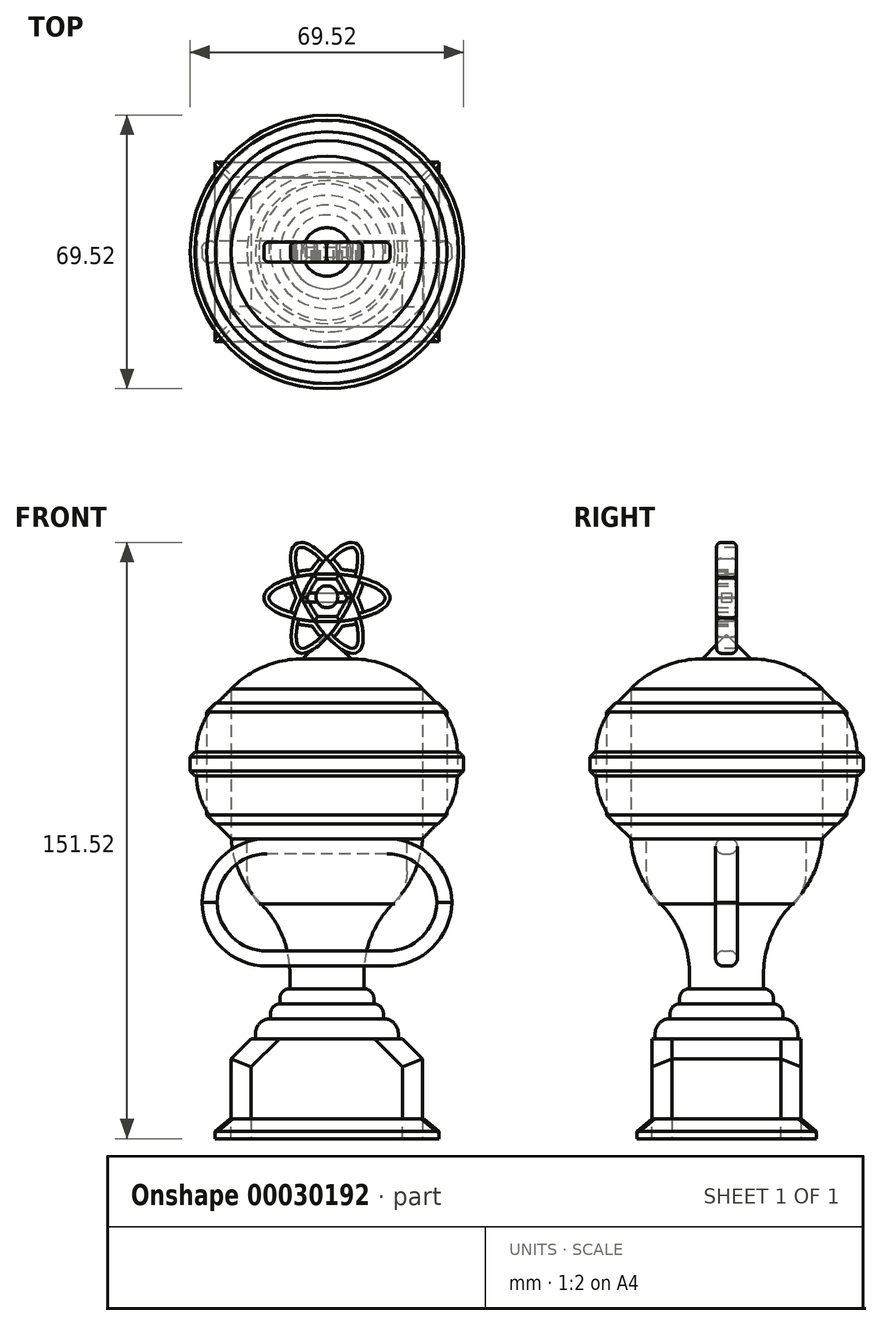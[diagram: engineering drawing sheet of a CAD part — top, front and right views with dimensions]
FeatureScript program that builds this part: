
annotation { "Feature Type Name" : "Feature", "Feature Type Description" : "" }
export const myFeature = defineFeature(function(context is Context, id is Id, definition is map)
    precondition{}
    {
        {
            var Q0;
            Q0=qCreatedBy(makeId("Top.planeOp"),FACE);
            var sketch = newSketch(context, id + "F0", { "sketchPlane" : qUnion([Q0])});
            skLineSegment(sketch, "E0.rect.bottom", {"start": v(-24.32, 18.93) * mm, "end": v(24.32, 18.93) * mm});
            skLineSegment(sketch, "E0.rect.top", {"start": v(-24.32, -18.93) * mm, "end": v(24.32, -18.93) * mm});
            skLineSegment(sketch, "E0.rect.left", {"start": v(-24.32, 18.93) * mm, "end": v(-24.32, -18.93) * mm});
            skLineSegment(sketch, "E0.rect.right", {"start": v(24.32, 18.93) * mm, "end": v(24.32, -18.93) * mm});
            skPoint(sketch, "E0.rect.middle", {"position": v(0, 0) * mm});
            skSolve(sketch);
        }
        {
            var Q0;
            Q0=makeQuery(id+"F0.imprint","IMPRINT",FACE,{"disambiguationData":[TD([[makeQuery(id+"F0.imprint","IMPRINT",EDGE,{"derivedFrom":sQuery(id+"F0.wireOp",EDGE,"E0.rect.bottom")}),-1.0]])]});
            extrude(context, id + "F1", {"entities" : qUnion([Q0]), "oppositeDirection" : true, "depth" : 76.2 * mm, "hasSecondDirection" : true, "secondDirectionOppositeDirection" : true, "secondDirectionDepth" : 50.8 * mm});
        }
        {
            var Q0;
            Q0=qCreatedBy(makeId("Top.planeOp"),FACE);
            var sketch = newSketch(context, id + "F2", { "sketchPlane" : qUnion([Q0])});
            skCircle(sketch, "E1", {"center": v(0, 0) * mm, "radius": 18.15 * mm});
            skSolve(sketch);
        }
        {
            var Q0;
            Q0=makeQuery(id+"F2.imprint","IMPRINT",FACE,{"disambiguationData":[TD([[makeQuery(id+"F2.imprint","IMPRINT",EDGE,{"derivedFrom":sQuery(id+"F2.wireOp",EDGE,"E1")}),1.0]])]});
            extrude(context, id + "F3", {"entities" : qUnion([Q0]), "operationType" : NewBodyOperationType.ADD, "oppositeDirection" : true, "depth" : 50.8 * mm, "hasSecondDirection" : true, "secondDirectionOppositeDirection" : true, "secondDirectionDepth" : 45.72 * mm});
        }
        {
            var Q0;
            Q0=makeQuery(id+"F3.opExtrude","CAP_EDGE",EDGE,{"disambiguationData":[OSD([sQuery(id+"F2.wireOp",EDGE,"E1")])],"isStart":true});
            fillet(context, id + "F4", {"entities" : qUnion([Q0]), "radius" : 3.8 * mm, "tangentPropagation" : true, "allowEdgeOverflow" : false});
        }
        {
            var Q0;
            Q0=makeQuery(id+"F3.opExtrude","CAP_FACE",FACE,{"disambiguationData":[OSD([sQuery(id+"F2.wireOp",EDGE,"E1")])],"isStart":true});
            extrude(context, id + "F5", {"entities" : qUnion([Q0]), "operationType" : NewBodyOperationType.ADD, "depth" : 3.8 * mm});
        }
        {
            var Q0;
            Q0=makeQuery(id+"F5.opExtrude","CAP_EDGE",EDGE,{"disambiguationData":[OSD([sQuery(id+"F2.wireOp",EDGE,"E1")])],"isStart":false});
            fillet(context, id + "F6", {"entities" : qUnion([Q0]), "radius" : 2.54 * mm, "tangentPropagation" : true, "allowEdgeOverflow" : false});
        }
        {
            var Q0;
            Q0=qCreatedBy(makeId("Top.planeOp"),FACE);
            var sketch = newSketch(context, id + "F7", { "sketchPlane" : qUnion([Q0])});
            skCircle(sketch, "E2", {"center": v(0, 0) * mm, "radius": 11.95 * mm});
            skSolve(sketch);
        }
        {
            var Q0;
            Q0=makeQuery(id+"F7.imprint","IMPRINT",FACE,{"disambiguationData":[TD([[makeQuery(id+"F7.imprint","IMPRINT",EDGE,{"derivedFrom":sQuery(id+"F7.wireOp",EDGE,"E2")}),1.0]])]});
            extrude(context, id + "F8", {"entities" : qUnion([Q0]), "operationType" : NewBodyOperationType.ADD, "oppositeDirection" : true, "depth" : 43.18 * mm, "hasSecondDirection" : true, "secondDirectionOppositeDirection" : true, "secondDirectionDepth" : 38.1 * mm});
        }
        {
            var Q0;
            Q0=makeQuery(id+"F8.opExtrude","CAP_EDGE",EDGE,{"disambiguationData":[OSD([sQuery(id+"F7.wireOp",EDGE,"E2")])],"isStart":true});
            fillet(context, id + "F9", {"entities" : qUnion([Q0]), "radius" : 2.54 * mm, "tangentPropagation" : true, "allowEdgeOverflow" : false});
        }
        {
            var Q0;
            Q0=qCreatedBy(makeId("Top.planeOp"),FACE);
            var sketch = newSketch(context, id + "F10", { "sketchPlane" : qUnion([Q0])});
            skCircle(sketch, "E3", {"center": v(0, 0) * mm, "radius": 24.35 * mm});
            skSolve(sketch);
        }
        {
            var Q0;
            Q0=makeQuery(id+"F8.opExtrude","CAP_FACE",FACE,{"disambiguationData":[OSD([sQuery(id+"F7.wireOp",EDGE,"E2")])],"isStart":true});
            extrude(context, id + "F11", {"entities" : qUnion([Q0]), "depth" : 15.24 * mm});
        }
        {
            var Q0;
            Q0=makeQuery(id+"F10.imprint","IMPRINT",FACE,{"disambiguationData":[TD([[makeQuery(id+"F10.imprint","IMPRINT",EDGE,{"derivedFrom":sQuery(id+"F10.wireOp",EDGE,"E3")}),1.0]])]});
            extrude(context, id + "F12", {"entities" : qUnion([Q0]), "operationType" : NewBodyOperationType.ADD, "oppositeDirection" : true, "depth" : 24.13 * mm, "hasDraft" : true, "draftAngle" : 0 * degree});
        }
        {
            var Q0;
            Q0=makeQuery(id+"F12.opExtrude","CAP_EDGE",EDGE,{"disambiguationData":[OSD([sQuery(id+"F10.wireOp",EDGE,"E3")])],"isStart":false});
            chamfer(context, id + "F13", {"entities" : qUnion([Q0]), "width" : 15.24 * mm, "tangentPropagation" : true});
        }
        {
            var Q0;
            {var subQ0=sQuery(id+"F10.wireOp",EDGE,"E3");Q0=makeQuery(id+"F13.opChamfer","BLEND_EDGE",EDGE,{"blendedFrom":[makeQuery(id+"F12.opExtrude","CAP_EDGE",EDGE,{"disambiguationData":[OSD([subQ0])],"isStart":false}),makeQuery(id+"F12.opExtrude","SWEPT_FACE",FACE,{"disambiguationData":[OSD([subQ0])]})],"blendedInto":[makeQuery(id+"F12.opExtrude","SWEPT_FACE",FACE,{"disambiguationData":[OSD([subQ0])]})]});}
            var Q1;
            Q1=makeQuery(id+"F13.opChamfer","BLEND_EDGE",EDGE,{"blendedFrom":[makeQuery(id+"F12.opExtrude","CAP_EDGE",EDGE,{"disambiguationData":[OSD([sQuery(id+"F10.wireOp",EDGE,"E3")])],"isStart":false}),makeQuery(id+"F11.opExtrude","SWEPT_FACE",FACE,{"disambiguationData":[OSD([sQuery(id+"F7.wireOp",EDGE,"E2")])]})],"blendedInto":[makeQuery(id+"F11.opExtrude","SWEPT_FACE",FACE,{"disambiguationData":[OSD([sQuery(id+"F7.wireOp",EDGE,"E2")])]})]});
            fillet(context, id + "F14", {"entities" : qUnion([Q0, Q1]), "radius" : 25.4 * mm, "tangentPropagation" : true, "allowEdgeOverflow" : false});
        }
        {
            var Q0;
            Q0=makeQuery(id+"F12.opExtrude","CAP_FACE",FACE,{"disambiguationData":[OSD([sQuery(id+"F10.wireOp",EDGE,"E3")])],"isStart":true});
            extrude(context, id + "F15", {"entities" : qUnion([Q0]), "depth" : 38.1 * mm});
        }
        {
            var Q0;
            Q0=makeQuery(id+"F15.opExtrude","CAP_FACE",FACE,{"disambiguationData":[OSD([sQuery(id+"F10.wireOp",EDGE,"E3")])],"isStart":false});
            extrude(context, id + "F16", {"entities" : qUnion([Q0]), "operationType" : NewBodyOperationType.ADD, "depth" : 7.62 * mm, "hasDraft" : true, "draftAngle" : 45 * degree, "draftPullDirection" : true});
        }
        {
            var Q0;
            Q0=makeQuery(id+"F16.opExtrude","CAP_EDGE",EDGE,{"disambiguationData":[OSD([sQuery(id+"F10.wireOp",EDGE,"E3")])],"isStart":false});
            fillet(context, id + "F17", {"entities" : qUnion([Q0]), "radius" : 25.4 * mm, "tangentPropagation" : true, "allowEdgeOverflow" : false});
        }
        {
            var Q0;
            Q0=qCreatedBy(makeId("Front.planeOp"),FACE);
            var sketch = newSketch(context, id + "F18", { "sketchPlane" : qUnion([Q0])});
            skEllipse(sketch, "E4", {"center": v(0, 61.22) * mm, "majorRadius": 16.03 * mm, "minorRadius": 6.08 * mm, "majorAxis": v(1, 0)});
            skEllipse(sketch, "E5", {"center": v(0, 61.22) * mm, "majorRadius": 15.7 * mm, "minorRadius": 5.85 * mm, "majorAxis": v(0.48, 0.88)});
            skEllipse(sketch, "E6", {"center": v(0, 61.22) * mm, "majorRadius": 15.84 * mm, "minorRadius": 5.77 * mm, "majorAxis": v(0.49, -0.87)});
            skSolve(sketch);
        }
        {
            var Q0;
            {var subQ0=sQuery(id+"F18.wireOp",EDGE,"E6");var subQ3=sQuery(id+"F18.wireOp",EDGE,"E4");var subQ4=makeQuery(id+"F18.imprint","INTERSECT",VERTEX,{"disambiguationData":[OD(0.0)],"derivedFrom":[subQ3,subQ0]});Q0=makeQuery(id+"F18.imprint","IMPRINT",FACE,{"disambiguationData":[TD([[makeQuery(id+"F18.imprint","IMPRINT",EDGE,{"disambiguationData":[TD([[subQ4,1.0]])],"derivedFrom":subQ3}),-1.0]])]});}
            var Q1;
            {var subQ0=sQuery(id+"F18.wireOp",EDGE,"E6");var subQ3=sQuery(id+"F18.wireOp",EDGE,"E4");var subQ7=makeQuery(id+"F18.imprint","INTERSECT",VERTEX,{"disambiguationData":[OD(2.0)],"derivedFrom":[subQ3,subQ0]});Q1=makeQuery(id+"F18.imprint","IMPRINT",FACE,{"disambiguationData":[TD([[makeQuery(id+"F18.imprint","IMPRINT",EDGE,{"disambiguationData":[TD([[subQ7,-1.0]])],"derivedFrom":subQ3}),1.0]])]});}
            var Q2;
            {var subQ1=sQuery(id+"F18.wireOp",EDGE,"E4");var subQ3=sQuery(id+"F18.wireOp",EDGE,"E5");var subQ5=makeQuery(id+"F18.imprint","INTERSECT",VERTEX,{"disambiguationData":[OD(0.0)],"derivedFrom":[subQ1,subQ3]});Q2=makeQuery(id+"F18.imprint","IMPRINT",FACE,{"disambiguationData":[TD([[makeQuery(id+"F18.imprint","IMPRINT",EDGE,{"disambiguationData":[TD([[subQ5,-1.0]])],"derivedFrom":subQ1}),-1.0]])]});}
            var Q3;
            {var subQ1=sQuery(id+"F18.wireOp",EDGE,"E5");var subQ3=sQuery(id+"F18.wireOp",EDGE,"E4");var subQ5=makeQuery(id+"F18.imprint","INTERSECT",VERTEX,{"disambiguationData":[OD(0.0)],"derivedFrom":[subQ3,subQ1]});Q3=makeQuery(id+"F18.imprint","IMPRINT",FACE,{"disambiguationData":[TD([[makeQuery(id+"F18.imprint","IMPRINT",EDGE,{"disambiguationData":[TD([[subQ5,1.0]])],"derivedFrom":subQ3}),1.0]])]});}
            var Q4;
            {var subQ0=sQuery(id+"F18.wireOp",EDGE,"E6");var subQ3=sQuery(id+"F18.wireOp",EDGE,"E4");var subQ4=makeQuery(id+"F18.imprint","INTERSECT",VERTEX,{"disambiguationData":[OD(1.0)],"derivedFrom":[subQ3,subQ0]});Q4=makeQuery(id+"F18.imprint","IMPRINT",FACE,{"disambiguationData":[TD([[makeQuery(id+"F18.imprint","IMPRINT",EDGE,{"disambiguationData":[TD([[subQ4,1.0]])],"derivedFrom":subQ3}),-1.0]])]});}
            var Q5;
            {var subQ1=sQuery(id+"F18.wireOp",EDGE,"E4");var subQ3=sQuery(id+"F18.wireOp",EDGE,"E5");var subQ5=makeQuery(id+"F18.imprint","INTERSECT",VERTEX,{"disambiguationData":[OD(1.0)],"derivedFrom":[subQ1,subQ3]});Q5=makeQuery(id+"F18.imprint","IMPRINT",FACE,{"disambiguationData":[TD([[makeQuery(id+"F18.imprint","IMPRINT",EDGE,{"disambiguationData":[TD([[subQ5,-1.0]])],"derivedFrom":subQ1}),-1.0]])]});}
            var Q6;
            {var subQ0=sQuery(id+"F18.wireOp",EDGE,"E6");var subQ3=sQuery(id+"F18.wireOp",EDGE,"E4");var subQ4=makeQuery(id+"F18.imprint","INTERSECT",VERTEX,{"disambiguationData":[OD(0.0)],"derivedFrom":[subQ3,subQ0]});Q6=makeQuery(id+"F18.imprint","IMPRINT",FACE,{"disambiguationData":[TD([[makeQuery(id+"F18.imprint","IMPRINT",EDGE,{"disambiguationData":[TD([[subQ4,-1.0]])],"derivedFrom":subQ3}),1.0]])]});}
            extrude(context, id + "F19", {"entities" : qUnion([Q0, Q1, Q2, Q3, Q4, Q5, Q6]), "endBound" : BoundingType.SYMMETRIC, "depth" : 5.08 * mm});
        }
        {
            var Q0;
            Q0=qCreatedBy(makeId("Top.planeOp"),FACE);
            var sketch = newSketch(context, id + "F20", { "sketchPlane" : qUnion([Q0])});
            skCircle(sketch, "E7", {"center": v(0, 0) * mm, "radius": 33.14 * mm});
            skSolve(sketch);
        }
        {
            var Q0;
            Q0=makeQuery(id+"F20.imprint","IMPRINT",FACE,{"disambiguationData":[TD([[makeQuery(id+"F20.imprint","IMPRINT",EDGE,{"derivedFrom":sQuery(id+"F20.wireOp",EDGE,"E7")}),1.0]])]});
            extrude(context, id + "F21", {"entities" : qUnion([Q0]), "depth" : 38.1 * mm});
        }
        {
            var Q0;
            Q0=makeQuery(id+"F21.opExtrude","CAP_EDGE",EDGE,{"disambiguationData":[OSD([sQuery(id+"F20.wireOp",EDGE,"E7")])],"isStart":false});
            var Q1;
            Q1=makeQuery(id+"F21.opExtrude","CAP_EDGE",EDGE,{"disambiguationData":[OSD([sQuery(id+"F20.wireOp",EDGE,"E7")])],"isStart":true});
            chamfer(context, id + "F22", {"entities" : qUnion([Q0, Q1]), "width" : 8.9 * mm, "tangentPropagation" : true});
        }
        {
            var Q0;
            {var subQ0=sQuery(id+"F20.wireOp",EDGE,"E7");Q0=makeQuery(id+"F22.opChamfer","BLEND_EDGE",EDGE,{"blendedFrom":[makeQuery(id+"F21.opExtrude","CAP_EDGE",EDGE,{"disambiguationData":[OSD([subQ0])],"isStart":false}),makeQuery(id+"F21.opExtrude","SWEPT_FACE",FACE,{"disambiguationData":[OSD([subQ0])]})],"blendedInto":[makeQuery(id+"F21.opExtrude","SWEPT_FACE",FACE,{"disambiguationData":[OSD([subQ0])]})]});}
            var Q1;
            {var subQ0=sQuery(id+"F20.wireOp",EDGE,"E7");Q1=makeQuery(id+"F22.opChamfer","BLEND_EDGE",EDGE,{"blendedFrom":[makeQuery(id+"F21.opExtrude","CAP_EDGE",EDGE,{"disambiguationData":[OSD([subQ0])],"isStart":true}),makeQuery(id+"F21.opExtrude","SWEPT_FACE",FACE,{"disambiguationData":[OSD([subQ0])]})],"blendedInto":[makeQuery(id+"F21.opExtrude","SWEPT_FACE",FACE,{"disambiguationData":[OSD([subQ0])]})]});}
            fillet(context, id + "F23", {"entities" : qUnion([Q0, Q1]), "radius" : 17.78 * mm, "tangentPropagation" : true, "allowEdgeOverflow" : false});
        }
        {
            var Q0;
            Q0=makeQuery(id+"F16.opExtrude","CAP_FACE",FACE,{"disambiguationData":[OSD([sQuery(id+"F10.wireOp",EDGE,"E3")])],"isStart":false});
            extrude(context, id + "F24", {"entities" : qUnion([Q0]), "depth" : 6.35 * mm, "hasDraft" : true, "draftAngle" : 45 * degree, "draftPullDirection" : true});
        }
        {
            var Q0;
            {var subQ0=sQuery(id+"F18.wireOp",EDGE,"E4");var subQ1=sQuery(id+"F18.wireOp",EDGE,"E5");var subQ2=sQuery(id+"F18.wireOp",EDGE,"E6");var subQ4=makeQuery(id+"F18.imprint","INTERSECT",VERTEX,{"disambiguationData":[OD(0.0)],"derivedFrom":[subQ0,subQ2]});var subQ5=makeQuery(id+"F18.imprint","INTERSECT",VERTEX,{"disambiguationData":[OD(0.0)],"derivedFrom":[subQ1,subQ2]});Q0=makeQuery(id+"F19.opExtrude","CAP_FACE",FACE,{"disambiguationData":[OSD([subQ0,subQ1,subQ2]),TDD([makeQuery(id+"F18.imprint","IMPRINT",EDGE,{"disambiguationData":[TD([[subQ4,1.0]])],"derivedFrom":subQ0}),makeQuery(id+"F18.imprint","IMPRINT",EDGE,{"disambiguationData":[TD([[subQ5,-1.0]])],"derivedFrom":subQ1}),makeQuery(id+"F18.imprint","IMPRINT",EDGE,{"disambiguationData":[TD([[subQ4,1.0]])],"derivedFrom":subQ2})])],"isStart":false});}
            var Q1;
            {var subQ0=sQuery(id+"F18.wireOp",EDGE,"E4");var subQ1=sQuery(id+"F18.wireOp",EDGE,"E5");var subQ2=sQuery(id+"F18.wireOp",EDGE,"E6");var subQ4=makeQuery(id+"F18.imprint","INTERSECT",VERTEX,{"disambiguationData":[OD(0.0)],"derivedFrom":[subQ0,subQ1]});var subQ5=makeQuery(id+"F18.imprint","INTERSECT",VERTEX,{"disambiguationData":[OD(0.0)],"derivedFrom":[subQ1,subQ2]});Q1=makeQuery(id+"F19.opExtrude","CAP_FACE",FACE,{"disambiguationData":[OSD([subQ0,subQ1,subQ2]),TDD([makeQuery(id+"F18.imprint","IMPRINT",EDGE,{"disambiguationData":[TD([[subQ4,-1.0]])],"derivedFrom":subQ0}),makeQuery(id+"F18.imprint","IMPRINT",EDGE,{"disambiguationData":[TD([[subQ4,-1.0]])],"derivedFrom":subQ1}),makeQuery(id+"F18.imprint","IMPRINT",EDGE,{"disambiguationData":[TD([[subQ5,1.0]])],"derivedFrom":subQ2})])],"isStart":false});}
            var Q2;
            {var subQ0=sQuery(id+"F18.wireOp",EDGE,"E4");var subQ1=sQuery(id+"F18.wireOp",EDGE,"E5");var subQ2=sQuery(id+"F18.wireOp",EDGE,"E6");var subQ3=makeQuery(id+"F18.imprint","INTERSECT",VERTEX,{"disambiguationData":[OD(2.0)],"derivedFrom":[subQ0,subQ1]});var subQ4=makeQuery(id+"F18.imprint","INTERSECT",VERTEX,{"disambiguationData":[OD(2.0)],"derivedFrom":[subQ0,subQ2]});var subQ5=makeQuery(id+"F18.imprint","INTERSECT",VERTEX,{"disambiguationData":[OD(3.0)],"derivedFrom":[subQ0,subQ1]});var subQ6=makeQuery(id+"F18.imprint","INTERSECT",VERTEX,{"disambiguationData":[OD(3.0)],"derivedFrom":[subQ0,subQ2]});Q2=makeQuery(id+"F19.opExtrude","CAP_FACE",FACE,{"disambiguationData":[OSD([subQ0,subQ1,subQ2]),TDD([makeQuery(id+"F18.imprint","IMPRINT",EDGE,{"disambiguationData":[TD([[subQ4,-1.0]])],"derivedFrom":subQ0}),makeQuery(id+"F18.imprint","IMPRINT",EDGE,{"disambiguationData":[TD([[subQ6,-1.0]])],"derivedFrom":subQ0}),makeQuery(id+"F18.imprint","IMPRINT",EDGE,{"disambiguationData":[TD([[subQ3,-1.0]])],"derivedFrom":subQ1}),makeQuery(id+"F18.imprint","IMPRINT",EDGE,{"disambiguationData":[TD([[subQ5,-1.0]])],"derivedFrom":subQ1}),makeQuery(id+"F18.imprint","IMPRINT",EDGE,{"disambiguationData":[TD([[subQ4,1.0]])],"derivedFrom":subQ2}),makeQuery(id+"F18.imprint","IMPRINT",EDGE,{"disambiguationData":[TD([[subQ6,1.0]])],"derivedFrom":subQ2})])],"isStart":false});}
            var Q3;
            {var subQ0=sQuery(id+"F18.wireOp",EDGE,"E4");var subQ1=sQuery(id+"F18.wireOp",EDGE,"E5");var subQ2=sQuery(id+"F18.wireOp",EDGE,"E6");var subQ4=makeQuery(id+"F18.imprint","INTERSECT",VERTEX,{"disambiguationData":[OD(1.0)],"derivedFrom":[subQ0,subQ1]});var subQ5=makeQuery(id+"F18.imprint","INTERSECT",VERTEX,{"disambiguationData":[OD(1.0)],"derivedFrom":[subQ1,subQ2]});Q3=makeQuery(id+"F19.opExtrude","CAP_FACE",FACE,{"disambiguationData":[OSD([subQ0,subQ1,subQ2]),TDD([makeQuery(id+"F18.imprint","IMPRINT",EDGE,{"disambiguationData":[TD([[subQ4,-1.0]])],"derivedFrom":subQ0}),makeQuery(id+"F18.imprint","IMPRINT",EDGE,{"disambiguationData":[TD([[subQ4,-1.0]])],"derivedFrom":subQ1}),makeQuery(id+"F18.imprint","IMPRINT",EDGE,{"disambiguationData":[TD([[subQ5,1.0]])],"derivedFrom":subQ2})])],"isStart":false});}
            var Q4;
            {var subQ0=sQuery(id+"F18.wireOp",EDGE,"E4");var subQ1=sQuery(id+"F18.wireOp",EDGE,"E5");var subQ2=sQuery(id+"F18.wireOp",EDGE,"E6");var subQ3=makeQuery(id+"F18.imprint","INTERSECT",VERTEX,{"disambiguationData":[OD(1.0)],"derivedFrom":[subQ0,subQ2]});var subQ4=makeQuery(id+"F18.imprint","INTERSECT",VERTEX,{"disambiguationData":[OD(0.0)],"derivedFrom":[subQ0,subQ1]});Q4=makeQuery(id+"F19.opExtrude","CAP_FACE",FACE,{"disambiguationData":[OSD([subQ0,subQ1,subQ2]),TDD([makeQuery(id+"F18.imprint","IMPRINT",EDGE,{"disambiguationData":[TD([[subQ4,1.0]])],"derivedFrom":subQ0}),makeQuery(id+"F18.imprint","IMPRINT",EDGE,{"disambiguationData":[TD([[subQ4,1.0]])],"derivedFrom":subQ1}),makeQuery(id+"F18.imprint","IMPRINT",EDGE,{"disambiguationData":[TD([[subQ3,-1.0]])],"derivedFrom":subQ2})])],"isStart":false});}
            var Q5;
            {var subQ0=sQuery(id+"F18.wireOp",EDGE,"E4");var subQ1=sQuery(id+"F18.wireOp",EDGE,"E5");var subQ2=sQuery(id+"F18.wireOp",EDGE,"E6");var subQ3=makeQuery(id+"F18.imprint","INTERSECT",VERTEX,{"disambiguationData":[OD(1.0)],"derivedFrom":[subQ0,subQ1]});var subQ4=makeQuery(id+"F18.imprint","INTERSECT",VERTEX,{"disambiguationData":[OD(0.0)],"derivedFrom":[subQ0,subQ2]});Q5=makeQuery(id+"F19.opExtrude","CAP_FACE",FACE,{"disambiguationData":[OSD([subQ0,subQ1,subQ2]),TDD([makeQuery(id+"F18.imprint","IMPRINT",EDGE,{"disambiguationData":[TD([[subQ4,-1.0]])],"derivedFrom":subQ0}),makeQuery(id+"F18.imprint","IMPRINT",EDGE,{"disambiguationData":[TD([[subQ3,1.0]])],"derivedFrom":subQ1}),makeQuery(id+"F18.imprint","IMPRINT",EDGE,{"disambiguationData":[TD([[subQ4,-1.0]])],"derivedFrom":subQ2})])],"isStart":true});}
            var Q6;
            {var subQ0=sQuery(id+"F18.wireOp",EDGE,"E4");var subQ1=sQuery(id+"F18.wireOp",EDGE,"E5");var subQ2=sQuery(id+"F18.wireOp",EDGE,"E6");var subQ4=makeQuery(id+"F18.imprint","INTERSECT",VERTEX,{"disambiguationData":[OD(0.0)],"derivedFrom":[subQ0,subQ2]});var subQ5=makeQuery(id+"F18.imprint","INTERSECT",VERTEX,{"disambiguationData":[OD(0.0)],"derivedFrom":[subQ1,subQ2]});Q6=makeQuery(id+"F19.opExtrude","CAP_FACE",FACE,{"disambiguationData":[OSD([subQ0,subQ1,subQ2]),TDD([makeQuery(id+"F18.imprint","IMPRINT",EDGE,{"disambiguationData":[TD([[subQ4,1.0]])],"derivedFrom":subQ0}),makeQuery(id+"F18.imprint","IMPRINT",EDGE,{"disambiguationData":[TD([[subQ5,-1.0]])],"derivedFrom":subQ1}),makeQuery(id+"F18.imprint","IMPRINT",EDGE,{"disambiguationData":[TD([[subQ4,1.0]])],"derivedFrom":subQ2})])],"isStart":true});}
            var Q7;
            {var subQ0=sQuery(id+"F18.wireOp",EDGE,"E4");var subQ1=sQuery(id+"F18.wireOp",EDGE,"E5");var subQ2=sQuery(id+"F18.wireOp",EDGE,"E6");var subQ4=makeQuery(id+"F18.imprint","INTERSECT",VERTEX,{"disambiguationData":[OD(0.0)],"derivedFrom":[subQ0,subQ1]});var subQ5=makeQuery(id+"F18.imprint","INTERSECT",VERTEX,{"disambiguationData":[OD(0.0)],"derivedFrom":[subQ1,subQ2]});Q7=makeQuery(id+"F19.opExtrude","CAP_FACE",FACE,{"disambiguationData":[OSD([subQ0,subQ1,subQ2]),TDD([makeQuery(id+"F18.imprint","IMPRINT",EDGE,{"disambiguationData":[TD([[subQ4,-1.0]])],"derivedFrom":subQ0}),makeQuery(id+"F18.imprint","IMPRINT",EDGE,{"disambiguationData":[TD([[subQ4,-1.0]])],"derivedFrom":subQ1}),makeQuery(id+"F18.imprint","IMPRINT",EDGE,{"disambiguationData":[TD([[subQ5,1.0]])],"derivedFrom":subQ2})])],"isStart":true});}
            var Q8;
            {var subQ0=sQuery(id+"F18.wireOp",EDGE,"E4");var subQ1=sQuery(id+"F18.wireOp",EDGE,"E5");var subQ2=sQuery(id+"F18.wireOp",EDGE,"E6");var subQ3=makeQuery(id+"F18.imprint","INTERSECT",VERTEX,{"disambiguationData":[OD(1.0)],"derivedFrom":[subQ0,subQ2]});var subQ4=makeQuery(id+"F18.imprint","INTERSECT",VERTEX,{"disambiguationData":[OD(0.0)],"derivedFrom":[subQ0,subQ1]});Q8=makeQuery(id+"F19.opExtrude","CAP_FACE",FACE,{"disambiguationData":[OSD([subQ0,subQ1,subQ2]),TDD([makeQuery(id+"F18.imprint","IMPRINT",EDGE,{"disambiguationData":[TD([[subQ4,1.0]])],"derivedFrom":subQ0}),makeQuery(id+"F18.imprint","IMPRINT",EDGE,{"disambiguationData":[TD([[subQ4,1.0]])],"derivedFrom":subQ1}),makeQuery(id+"F18.imprint","IMPRINT",EDGE,{"disambiguationData":[TD([[subQ3,-1.0]])],"derivedFrom":subQ2})])],"isStart":true});}
            var Q9;
            {var subQ0=sQuery(id+"F18.wireOp",EDGE,"E4");var subQ1=sQuery(id+"F18.wireOp",EDGE,"E5");var subQ2=sQuery(id+"F18.wireOp",EDGE,"E6");var subQ4=makeQuery(id+"F18.imprint","INTERSECT",VERTEX,{"disambiguationData":[OD(1.0)],"derivedFrom":[subQ0,subQ2]});var subQ5=makeQuery(id+"F18.imprint","INTERSECT",VERTEX,{"disambiguationData":[OD(1.0)],"derivedFrom":[subQ1,subQ2]});Q9=makeQuery(id+"F19.opExtrude","CAP_FACE",FACE,{"disambiguationData":[OSD([subQ0,subQ1,subQ2]),TDD([makeQuery(id+"F18.imprint","IMPRINT",EDGE,{"disambiguationData":[TD([[subQ4,1.0]])],"derivedFrom":subQ0}),makeQuery(id+"F18.imprint","IMPRINT",EDGE,{"disambiguationData":[TD([[subQ5,-1.0]])],"derivedFrom":subQ1}),makeQuery(id+"F18.imprint","IMPRINT",EDGE,{"disambiguationData":[TD([[subQ4,1.0]])],"derivedFrom":subQ2})])],"isStart":true});}
            var Q10;
            {var subQ0=sQuery(id+"F18.wireOp",EDGE,"E4");var subQ1=sQuery(id+"F18.wireOp",EDGE,"E5");var subQ2=sQuery(id+"F18.wireOp",EDGE,"E6");var subQ4=makeQuery(id+"F18.imprint","INTERSECT",VERTEX,{"disambiguationData":[OD(1.0)],"derivedFrom":[subQ0,subQ1]});var subQ5=makeQuery(id+"F18.imprint","INTERSECT",VERTEX,{"disambiguationData":[OD(1.0)],"derivedFrom":[subQ1,subQ2]});Q10=makeQuery(id+"F19.opExtrude","CAP_FACE",FACE,{"disambiguationData":[OSD([subQ0,subQ1,subQ2]),TDD([makeQuery(id+"F18.imprint","IMPRINT",EDGE,{"disambiguationData":[TD([[subQ4,-1.0]])],"derivedFrom":subQ0}),makeQuery(id+"F18.imprint","IMPRINT",EDGE,{"disambiguationData":[TD([[subQ4,-1.0]])],"derivedFrom":subQ1}),makeQuery(id+"F18.imprint","IMPRINT",EDGE,{"disambiguationData":[TD([[subQ5,1.0]])],"derivedFrom":subQ2})])],"isStart":true});}
            var Q11;
            {var subQ0=sQuery(id+"F18.wireOp",EDGE,"E4");var subQ1=sQuery(id+"F18.wireOp",EDGE,"E5");var subQ2=sQuery(id+"F18.wireOp",EDGE,"E6");var subQ3=makeQuery(id+"F18.imprint","INTERSECT",VERTEX,{"disambiguationData":[OD(2.0)],"derivedFrom":[subQ0,subQ1]});var subQ4=makeQuery(id+"F18.imprint","INTERSECT",VERTEX,{"disambiguationData":[OD(2.0)],"derivedFrom":[subQ0,subQ2]});var subQ5=makeQuery(id+"F18.imprint","INTERSECT",VERTEX,{"disambiguationData":[OD(3.0)],"derivedFrom":[subQ0,subQ1]});var subQ6=makeQuery(id+"F18.imprint","INTERSECT",VERTEX,{"disambiguationData":[OD(3.0)],"derivedFrom":[subQ0,subQ2]});Q11=makeQuery(id+"F19.opExtrude","CAP_FACE",FACE,{"disambiguationData":[OSD([subQ0,subQ1,subQ2]),TDD([makeQuery(id+"F18.imprint","IMPRINT",EDGE,{"disambiguationData":[TD([[subQ4,-1.0]])],"derivedFrom":subQ0}),makeQuery(id+"F18.imprint","IMPRINT",EDGE,{"disambiguationData":[TD([[subQ6,-1.0]])],"derivedFrom":subQ0}),makeQuery(id+"F18.imprint","IMPRINT",EDGE,{"disambiguationData":[TD([[subQ3,-1.0]])],"derivedFrom":subQ1}),makeQuery(id+"F18.imprint","IMPRINT",EDGE,{"disambiguationData":[TD([[subQ5,-1.0]])],"derivedFrom":subQ1}),makeQuery(id+"F18.imprint","IMPRINT",EDGE,{"disambiguationData":[TD([[subQ4,1.0]])],"derivedFrom":subQ2}),makeQuery(id+"F18.imprint","IMPRINT",EDGE,{"disambiguationData":[TD([[subQ6,1.0]])],"derivedFrom":subQ2})])],"isStart":true});}
            var Q12;
            {var subQ0=sQuery(id+"F18.wireOp",EDGE,"E4");var subQ1=sQuery(id+"F18.wireOp",EDGE,"E5");var subQ2=sQuery(id+"F18.wireOp",EDGE,"E6");var subQ3=makeQuery(id+"F18.imprint","INTERSECT",VERTEX,{"disambiguationData":[OD(1.0)],"derivedFrom":[subQ0,subQ1]});var subQ4=makeQuery(id+"F18.imprint","INTERSECT",VERTEX,{"disambiguationData":[OD(0.0)],"derivedFrom":[subQ0,subQ2]});Q12=makeQuery(id+"F19.opExtrude","CAP_FACE",FACE,{"disambiguationData":[OSD([subQ0,subQ1,subQ2]),TDD([makeQuery(id+"F18.imprint","IMPRINT",EDGE,{"disambiguationData":[TD([[subQ4,-1.0]])],"derivedFrom":subQ0}),makeQuery(id+"F18.imprint","IMPRINT",EDGE,{"disambiguationData":[TD([[subQ3,1.0]])],"derivedFrom":subQ1}),makeQuery(id+"F18.imprint","IMPRINT",EDGE,{"disambiguationData":[TD([[subQ4,-1.0]])],"derivedFrom":subQ2})])],"isStart":false});}
            var Q13;
            {var subQ0=sQuery(id+"F18.wireOp",EDGE,"E4");var subQ1=sQuery(id+"F18.wireOp",EDGE,"E5");var subQ2=sQuery(id+"F18.wireOp",EDGE,"E6");var subQ4=makeQuery(id+"F18.imprint","INTERSECT",VERTEX,{"disambiguationData":[OD(1.0)],"derivedFrom":[subQ0,subQ2]});var subQ5=makeQuery(id+"F18.imprint","INTERSECT",VERTEX,{"disambiguationData":[OD(1.0)],"derivedFrom":[subQ1,subQ2]});Q13=makeQuery(id+"F19.opExtrude","CAP_FACE",FACE,{"disambiguationData":[OSD([subQ0,subQ1,subQ2]),TDD([makeQuery(id+"F18.imprint","IMPRINT",EDGE,{"disambiguationData":[TD([[subQ4,1.0]])],"derivedFrom":subQ0}),makeQuery(id+"F18.imprint","IMPRINT",EDGE,{"disambiguationData":[TD([[subQ5,-1.0]])],"derivedFrom":subQ1}),makeQuery(id+"F18.imprint","IMPRINT",EDGE,{"disambiguationData":[TD([[subQ4,1.0]])],"derivedFrom":subQ2})])],"isStart":false});}
            shell(context, id + "F25", {"entities" : qUnion([Q0, Q1, Q2, Q3, Q4, Q5, Q6, Q7, Q8, Q9, Q10, Q11, Q12, Q13]), "thickness" : 1.27 * mm});
        }
        {
            var Q0;
            Q0=qCreatedBy(makeId("Right.planeOp"),FACE);
            var sketch = newSketch(context, id + "F26", { "sketchPlane" : qUnion([Q0])});
            skLineSegment(sketch, "E8.rect.bottom", {"start": v(2.76, 0) * mm, "end": v(-2.76, 0) * mm});
            skLineSegment(sketch, "E8.rect.top", {"start": v(2.76, -32.34) * mm, "end": v(-2.76, -32.34) * mm});
            skLineSegment(sketch, "E8.rect.left", {"start": v(2.76, 0) * mm, "end": v(2.76, -32.34) * mm});
            skLineSegment(sketch, "E8.rect.right", {"start": v(-2.76, 0) * mm, "end": v(-2.76, -32.34) * mm});
            skPoint(sketch, "E8.rect.middle", {"position": v(0, -16.17) * mm});
            skSolve(sketch);
        }
        {
            var Q0;
            Q0=makeQuery(id+"F26.imprint","IMPRINT",FACE,{"disambiguationData":[TD([[makeQuery(id+"F26.imprint","IMPRINT",EDGE,{"derivedFrom":sQuery(id+"F26.wireOp",EDGE,"E8.rect.bottom")}),1.0]])]});
            extrude(context, id + "F27", {"entities" : qUnion([Q0]), "endBound" : BoundingType.SYMMETRIC, "depth" : 63.5 * mm});
        }
        {
            var Q0;
            Q0=makeQuery(id+"F27.opExtrude","CAP_EDGE",EDGE,{"disambiguationData":[OSD([sQuery(id+"F26.wireOp",EDGE,"E8.rect.bottom")])],"isStart":true});
            var Q1;
            Q1=makeQuery(id+"F27.opExtrude","CAP_EDGE",EDGE,{"disambiguationData":[OSD([sQuery(id+"F26.wireOp",EDGE,"E8.rect.top")])],"isStart":true});
            var Q2;
            Q2=makeQuery(id+"F27.opExtrude","CAP_EDGE",EDGE,{"disambiguationData":[OSD([sQuery(id+"F26.wireOp",EDGE,"E8.rect.bottom")])],"isStart":false});
            var Q3;
            Q3=makeQuery(id+"F27.opExtrude","CAP_EDGE",EDGE,{"disambiguationData":[OSD([sQuery(id+"F26.wireOp",EDGE,"E8.rect.top")])],"isStart":false});
            fillet(context, id + "F28", {"entities" : qUnion([Q0, Q1, Q2, Q3]), "radius" : 16.5 * mm, "tangentPropagation" : true, "allowEdgeOverflow" : false});
        }
        {
            var Q0;
            Q0=makeQuery(id+"F27.opExtrude","SWEPT_FACE",FACE,{"disambiguationData":[OSD([sQuery(id+"F26.wireOp",EDGE,"E8.rect.right")])]});
            var Q1;
            Q1=makeQuery(id+"F27.opExtrude","SWEPT_FACE",FACE,{"disambiguationData":[OSD([sQuery(id+"F26.wireOp",EDGE,"E8.rect.left")])]});
            shell(context, id + "F29", {"entities" : qUnion([Q0, Q1]), "thickness" : 3.8 * mm});
        }
        {
            var Q0;
            Q0=qCreatedBy(makeId("Top.planeOp"),FACE);
            var sketch = newSketch(context, id + "F30", { "sketchPlane" : qUnion([Q0])});
            skLineSegment(sketch, "E9.rect.bottom", {"start": v(-28.47, -22.8) * mm, "end": v(28.47, -22.8) * mm});
            skLineSegment(sketch, "E9.rect.top", {"start": v(-28.47, 22.8) * mm, "end": v(28.47, 22.8) * mm});
            skLineSegment(sketch, "E9.rect.left", {"start": v(-28.47, -22.8) * mm, "end": v(-28.47, 22.8) * mm});
            skLineSegment(sketch, "E9.rect.right", {"start": v(28.47, -22.8) * mm, "end": v(28.47, 22.8) * mm});
            skPoint(sketch, "E9.rect.middle", {"position": v(0, 0) * mm});
            skSolve(sketch);
        }
        {
            var Q0;
            Q0=makeQuery(id+"F30.imprint","IMPRINT",FACE,{"disambiguationData":[TD([[makeQuery(id+"F30.imprint","IMPRINT",EDGE,{"derivedFrom":sQuery(id+"F30.wireOp",EDGE,"E9.rect.bottom")}),1.0]])]});
            extrude(context, id + "F31", {"entities" : qUnion([Q0]), "oppositeDirection" : true, "depth" : 76.2 * mm, "hasSecondDirection" : true, "secondDirectionOppositeDirection" : true, "secondDirectionDepth" : 71.12 * mm});
        }
        {
            var Q0;
            Q0=makeQuery(id+"F31.opExtrude","CAP_EDGE",EDGE,{"disambiguationData":[OSD([sQuery(id+"F30.wireOp",EDGE,"E9.rect.bottom")])],"isStart":true});
            var Q1;
            Q1=makeQuery(id+"F31.opExtrude","CAP_EDGE",EDGE,{"disambiguationData":[OSD([sQuery(id+"F30.wireOp",EDGE,"E9.rect.left")])],"isStart":true});
            var Q2;
            Q2=makeQuery(id+"F31.opExtrude","CAP_EDGE",EDGE,{"disambiguationData":[OSD([sQuery(id+"F30.wireOp",EDGE,"E9.rect.right")])],"isStart":true});
            var Q3;
            Q3=makeQuery(id+"F31.opExtrude","CAP_EDGE",EDGE,{"disambiguationData":[OSD([sQuery(id+"F30.wireOp",EDGE,"E9.rect.top")])],"isStart":true});
            chamfer(context, id + "F32", {"entities" : qUnion([Q0, Q1, Q2, Q3]), "chamferType" : ChamferType.OFFSET_ANGLE, "width" : 3.8 * mm, "oppositeDirection" : false, "angle" : 40 * degree, "tangentPropagation" : true});
        }
        {
            var Q0;
            Q0=makeQuery(id+"F1.opExtrude","CAP_EDGE",EDGE,{"disambiguationData":[OSD([sQuery(id+"F0.wireOp",EDGE,"E0.rect.left")])],"isStart":true});
            var Q1;
            Q1=makeQuery(id+"F1.opExtrude","CAP_EDGE",EDGE,{"disambiguationData":[OSD([sQuery(id+"F0.wireOp",EDGE,"E0.rect.right")])],"isStart":true});
            chamfer(context, id + "F33", {"entities" : qUnion([Q0, Q1]), "width" : 5.08 * mm, "tangentPropagation" : true});
        }
        {
            var Q0;
            Q0=makeQuery(id+"F33.opChamfer","BLEND_EDGE",EDGE,{"blendedFrom":[makeQuery(id+"F1.opExtrude","CAP_EDGE",EDGE,{"disambiguationData":[OSD([sQuery(id+"F0.wireOp",EDGE,"E0.rect.left")])],"isStart":true}),makeQuery(id+"F1.opExtrude","SWEPT_FACE",FACE,{"disambiguationData":[OSD([sQuery(id+"F0.wireOp",EDGE,"E0.rect.top")])]})],"blendedInto":[makeQuery(id+"F1.opExtrude","SWEPT_FACE",FACE,{"disambiguationData":[OSD([sQuery(id+"F0.wireOp",EDGE,"E0.rect.top")])]})]});
            var Q1;
            Q1=makeQuery(id+"F33.opChamfer","BLEND_EDGE",EDGE,{"blendedFrom":[makeQuery(id+"F1.opExtrude","CAP_EDGE",EDGE,{"disambiguationData":[OSD([sQuery(id+"F0.wireOp",EDGE,"E0.rect.right")])],"isStart":true}),makeQuery(id+"F1.opExtrude","SWEPT_FACE",FACE,{"disambiguationData":[OSD([sQuery(id+"F0.wireOp",EDGE,"E0.rect.top")])]})],"blendedInto":[makeQuery(id+"F1.opExtrude","SWEPT_FACE",FACE,{"disambiguationData":[OSD([sQuery(id+"F0.wireOp",EDGE,"E0.rect.top")])]})]});
            var Q2;
            Q2=makeQuery(id+"F33.opChamfer","BLEND_EDGE",EDGE,{"blendedFrom":[makeQuery(id+"F1.opExtrude","CAP_EDGE",EDGE,{"disambiguationData":[OSD([sQuery(id+"F0.wireOp",EDGE,"E0.rect.left")])],"isStart":true}),makeQuery(id+"F1.opExtrude","SWEPT_FACE",FACE,{"disambiguationData":[OSD([sQuery(id+"F0.wireOp",EDGE,"E0.rect.bottom")])]})],"blendedInto":[makeQuery(id+"F1.opExtrude","SWEPT_FACE",FACE,{"disambiguationData":[OSD([sQuery(id+"F0.wireOp",EDGE,"E0.rect.bottom")])]})]});
            var Q3;
            Q3=makeQuery(id+"F33.opChamfer","BLEND_EDGE",EDGE,{"blendedFrom":[makeQuery(id+"F1.opExtrude","CAP_EDGE",EDGE,{"disambiguationData":[OSD([sQuery(id+"F0.wireOp",EDGE,"E0.rect.right")])],"isStart":true}),makeQuery(id+"F1.opExtrude","SWEPT_FACE",FACE,{"disambiguationData":[OSD([sQuery(id+"F0.wireOp",EDGE,"E0.rect.bottom")])]})],"blendedInto":[makeQuery(id+"F1.opExtrude","SWEPT_FACE",FACE,{"disambiguationData":[OSD([sQuery(id+"F0.wireOp",EDGE,"E0.rect.bottom")])]})]});
            chamfer(context, id + "F34", {"entities" : qUnion([Q0, Q1, Q2, Q3]), "width" : 5.08 * mm, "tangentPropagation" : true});
        }
        {
            var Q0;
            Q0=qCreatedBy(makeId("Top.planeOp"),FACE);
            var sketch = newSketch(context, id + "F35", { "sketchPlane" : qUnion([Q0])});
            skCircle(sketch, "E10", {"center": v(0, 0) * mm, "radius": 20.32 * mm});
            skSolve(sketch);
        }
        {
            var Q0;
            Q0=makeQuery(id+"F35.imprint","IMPRINT",FACE,{"disambiguationData":[TD([[makeQuery(id+"F35.imprint","IMPRINT",EDGE,{"derivedFrom":sQuery(id+"F35.wireOp",EDGE,"E10")}),1.0]])]});
            extrude(context, id + "F36", {"entities" : qUnion([Q0]), "oppositeDirection" : true, "depth" : 16.5 * mm});
        }
        {
            var Q0;
            Q0=qCreatedBy(makeId("Top.planeOp"),FACE);
            var sketch = newSketch(context, id + "F37", { "sketchPlane" : qUnion([Q0])});
            skCircle(sketch, "E11", {"center": v(0, 0) * mm, "radius": 30.54 * mm});
            skSolve(sketch);
        }
        {
            var Q0;
            Q0=makeQuery(id+"F37.imprint","IMPRINT",FACE,{"disambiguationData":[TD([[makeQuery(id+"F37.imprint","IMPRINT",EDGE,{"derivedFrom":sQuery(id+"F37.wireOp",EDGE,"E11")}),1.0]])]});
            extrude(context, id + "F38", {"entities" : qUnion([Q0]), "depth" : 34.54 * mm, "hasSecondDirection" : true, "secondDirectionOppositeDirection" : false, "secondDirectionDepth" : 3.8 * mm});
        }
        {
            var Q0;
            Q0=qCreatedBy(makeId("Top.planeOp"),FACE);
            var sketch = newSketch(context, id + "F39", { "sketchPlane" : qUnion([Q0])});
            skCircle(sketch, "E12", {"center": v(0, 0) * mm, "radius": 34.76 * mm});
            skSolve(sketch);
        }
        {
            var Q0;
            Q0=makeQuery(id+"F39.imprint","IMPRINT",FACE,{"disambiguationData":[TD([[makeQuery(id+"F39.imprint","IMPRINT",EDGE,{"derivedFrom":sQuery(id+"F39.wireOp",EDGE,"E12")}),1.0]])]});
            extrude(context, id + "F40", {"entities" : qUnion([Q0]), "depth" : 22.1 * mm, "hasSecondDirection" : true, "secondDirectionOppositeDirection" : false, "secondDirectionDepth" : 16 * mm});
        }
        {
            var Q0;
            {var subQ0=sQuery(id+"F18.wireOp",EDGE,"E6");Q0=makeQuery(id+"F19.opExtrude","CAP_EDGE",EDGE,{"disambiguationData":[OSD([subQ0]),TDD([makeQuery(id+"F18.imprint","IMPRINT",EDGE,{"disambiguationData":[TD([[makeQuery(id+"F18.imprint","INTERSECT",VERTEX,{"disambiguationData":[OD(0.0)],"derivedFrom":[sQuery(id+"F18.wireOp",EDGE,"E4"),subQ0]}),1.0]])],"derivedFrom":subQ0})])],"isStart":false});}
            var Q1;
            {var subQ0=sQuery(id+"F18.wireOp",EDGE,"E5");Q1=makeQuery(id+"F19.opExtrude","CAP_EDGE",EDGE,{"disambiguationData":[OSD([subQ0]),TDD([makeQuery(id+"F18.imprint","IMPRINT",EDGE,{"disambiguationData":[TD([[makeQuery(id+"F18.imprint","INTERSECT",VERTEX,{"disambiguationData":[OD(0.0)],"derivedFrom":[sQuery(id+"F18.wireOp",EDGE,"E4"),subQ0]}),-1.0]])],"derivedFrom":subQ0})])],"isStart":true});}
            var Q2;
            {var subQ0=sQuery(id+"F18.wireOp",EDGE,"E5");Q2=makeQuery(id+"F19.opExtrude","CAP_EDGE",EDGE,{"disambiguationData":[OSD([subQ0]),TDD([makeQuery(id+"F18.imprint","IMPRINT",EDGE,{"disambiguationData":[TD([[makeQuery(id+"F18.imprint","INTERSECT",VERTEX,{"disambiguationData":[OD(0.0)],"derivedFrom":[sQuery(id+"F18.wireOp",EDGE,"E4"),subQ0]}),-1.0]])],"derivedFrom":subQ0})])],"isStart":false});}
            var Q3;
            {var subQ0=sQuery(id+"F18.wireOp",EDGE,"E6");Q3=makeQuery(id+"F19.opExtrude","CAP_EDGE",EDGE,{"disambiguationData":[OSD([subQ0]),TDD([makeQuery(id+"F18.imprint","IMPRINT",EDGE,{"disambiguationData":[TD([[makeQuery(id+"F18.imprint","INTERSECT",VERTEX,{"disambiguationData":[OD(0.0)],"derivedFrom":[sQuery(id+"F18.wireOp",EDGE,"E4"),subQ0]}),1.0]])],"derivedFrom":subQ0})])],"isStart":true});}
            var Q4;
            {var subQ0=sQuery(id+"F18.wireOp",EDGE,"E4");Q4=makeQuery(id+"F19.opExtrude","CAP_EDGE",EDGE,{"disambiguationData":[OSD([subQ0]),TDD([makeQuery(id+"F18.imprint","IMPRINT",EDGE,{"disambiguationData":[TD([[makeQuery(id+"F18.imprint","INTERSECT",VERTEX,{"disambiguationData":[OD(0.0)],"derivedFrom":[subQ0,sQuery(id+"F18.wireOp",EDGE,"E6")]}),-1.0]])],"derivedFrom":subQ0})])],"isStart":true});}
            var Q5;
            {var subQ0=sQuery(id+"F18.wireOp",EDGE,"E4");Q5=makeQuery(id+"F19.opExtrude","CAP_EDGE",EDGE,{"disambiguationData":[OSD([subQ0]),TDD([makeQuery(id+"F18.imprint","IMPRINT",EDGE,{"disambiguationData":[TD([[makeQuery(id+"F18.imprint","INTERSECT",VERTEX,{"disambiguationData":[OD(0.0)],"derivedFrom":[subQ0,sQuery(id+"F18.wireOp",EDGE,"E6")]}),-1.0]])],"derivedFrom":subQ0})])],"isStart":false});}
            var Q6;
            {var subQ0=sQuery(id+"F18.wireOp",EDGE,"E5");Q6=makeQuery(id+"F19.opExtrude","CAP_EDGE",EDGE,{"disambiguationData":[OSD([subQ0]),TDD([makeQuery(id+"F18.imprint","IMPRINT",EDGE,{"disambiguationData":[TD([[makeQuery(id+"F18.imprint","INTERSECT",VERTEX,{"disambiguationData":[OD(1.0)],"derivedFrom":[sQuery(id+"F18.wireOp",EDGE,"E4"),subQ0]}),-1.0]])],"derivedFrom":subQ0})])],"isStart":true});}
            var Q7;
            {var subQ0=sQuery(id+"F18.wireOp",EDGE,"E6");Q7=makeQuery(id+"F19.opExtrude","CAP_EDGE",EDGE,{"disambiguationData":[OSD([subQ0]),TDD([makeQuery(id+"F18.imprint","IMPRINT",EDGE,{"disambiguationData":[TD([[makeQuery(id+"F18.imprint","INTERSECT",VERTEX,{"disambiguationData":[OD(1.0)],"derivedFrom":[sQuery(id+"F18.wireOp",EDGE,"E4"),subQ0]}),1.0]])],"derivedFrom":subQ0})])],"isStart":false});}
            var Q8;
            {var subQ0=sQuery(id+"F18.wireOp",EDGE,"E6");Q8=makeQuery(id+"F19.opExtrude","CAP_EDGE",EDGE,{"disambiguationData":[OSD([subQ0]),TDD([makeQuery(id+"F18.imprint","IMPRINT",EDGE,{"disambiguationData":[TD([[makeQuery(id+"F18.imprint","INTERSECT",VERTEX,{"disambiguationData":[OD(1.0)],"derivedFrom":[sQuery(id+"F18.wireOp",EDGE,"E4"),subQ0]}),1.0]])],"derivedFrom":subQ0})])],"isStart":true});}
            var Q9;
            {var subQ0=sQuery(id+"F18.wireOp",EDGE,"E4");Q9=makeQuery(id+"F19.opExtrude","CAP_EDGE",EDGE,{"disambiguationData":[OSD([subQ0]),TDD([makeQuery(id+"F18.imprint","IMPRINT",EDGE,{"disambiguationData":[TD([[makeQuery(id+"F18.imprint","INTERSECT",VERTEX,{"disambiguationData":[OD(0.0)],"derivedFrom":[subQ0,sQuery(id+"F18.wireOp",EDGE,"E5")]}),1.0]])],"derivedFrom":subQ0})])],"isStart":false});}
            var Q10;
            {var subQ0=sQuery(id+"F18.wireOp",EDGE,"E4");Q10=makeQuery(id+"F19.opExtrude","CAP_EDGE",EDGE,{"disambiguationData":[OSD([subQ0]),TDD([makeQuery(id+"F18.imprint","IMPRINT",EDGE,{"disambiguationData":[TD([[makeQuery(id+"F18.imprint","INTERSECT",VERTEX,{"disambiguationData":[OD(0.0)],"derivedFrom":[subQ0,sQuery(id+"F18.wireOp",EDGE,"E5")]}),1.0]])],"derivedFrom":subQ0})])],"isStart":true});}
            var Q11;
            {var subQ0=sQuery(id+"F18.wireOp",EDGE,"E5");Q11=makeQuery(id+"F19.opExtrude","CAP_EDGE",EDGE,{"disambiguationData":[OSD([subQ0]),TDD([makeQuery(id+"F18.imprint","IMPRINT",EDGE,{"disambiguationData":[TD([[makeQuery(id+"F18.imprint","INTERSECT",VERTEX,{"disambiguationData":[OD(1.0)],"derivedFrom":[sQuery(id+"F18.wireOp",EDGE,"E4"),subQ0]}),-1.0]])],"derivedFrom":subQ0})])],"isStart":false});}
            fillet(context, id + "F41", {"entities" : qUnion([Q0, Q1, Q2, Q3, Q4, Q5, Q6, Q7, Q8, Q9, Q10, Q11]), "radius" : 1.27 * mm, "tangentPropagation" : true, "allowEdgeOverflow" : false});
        }
        {
            var Q0;
            {var subQ0=sQuery(id+"F18.wireOp",EDGE,"E6");var subQ3=sQuery(id+"F18.wireOp",EDGE,"E4");var subQ4=makeQuery(id+"F18.imprint","INTERSECT",VERTEX,{"disambiguationData":[OD(0.0)],"derivedFrom":[subQ3,subQ0]});Q0=makeQuery(id+"F18.imprint","IMPRINT",FACE,{"disambiguationData":[TD([[makeQuery(id+"F18.imprint","IMPRINT",EDGE,{"disambiguationData":[TD([[subQ4,1.0]])],"derivedFrom":subQ3}),1.0]])]});}
            var Q1;
            {var subQ0=sQuery(id+"F18.wireOp",EDGE,"E6");var subQ1=sQuery(id+"F18.wireOp",EDGE,"E4");var subQ2=makeQuery(id+"F18.imprint","INTERSECT",VERTEX,{"disambiguationData":[OD(2.0)],"derivedFrom":[subQ1,subQ0]});Q1=makeQuery(id+"F18.imprint","IMPRINT",FACE,{"disambiguationData":[TD([[makeQuery(id+"F18.imprint","IMPRINT",EDGE,{"disambiguationData":[TD([[subQ2,-1.0]])],"derivedFrom":subQ1}),-1.0]])]});}
            var Q2;
            {var subQ1=sQuery(id+"F18.wireOp",EDGE,"E5");var subQ3=sQuery(id+"F18.wireOp",EDGE,"E4");var subQ5=makeQuery(id+"F18.imprint","INTERSECT",VERTEX,{"disambiguationData":[OD(0.0)],"derivedFrom":[subQ3,subQ1]});Q2=makeQuery(id+"F18.imprint","IMPRINT",FACE,{"disambiguationData":[TD([[makeQuery(id+"F18.imprint","IMPRINT",EDGE,{"disambiguationData":[TD([[subQ5,-1.0]])],"derivedFrom":subQ3}),1.0]])]});}
            var Q3;
            {var subQ0=sQuery(id+"F18.wireOp",EDGE,"E6");var subQ3=sQuery(id+"F18.wireOp",EDGE,"E4");var subQ4=makeQuery(id+"F18.imprint","INTERSECT",VERTEX,{"disambiguationData":[OD(1.0)],"derivedFrom":[subQ3,subQ0]});Q3=makeQuery(id+"F18.imprint","IMPRINT",FACE,{"disambiguationData":[TD([[makeQuery(id+"F18.imprint","IMPRINT",EDGE,{"disambiguationData":[TD([[subQ4,1.0]])],"derivedFrom":subQ3}),1.0]])]});}
            var Q4;
            {var subQ0=sQuery(id+"F18.wireOp",EDGE,"E6");var subQ1=sQuery(id+"F18.wireOp",EDGE,"E4");var subQ2=makeQuery(id+"F18.imprint","INTERSECT",VERTEX,{"disambiguationData":[OD(3.0)],"derivedFrom":[subQ1,subQ0]});Q4=makeQuery(id+"F18.imprint","IMPRINT",FACE,{"disambiguationData":[TD([[makeQuery(id+"F18.imprint","IMPRINT",EDGE,{"disambiguationData":[TD([[subQ2,-1.0]])],"derivedFrom":subQ1}),-1.0]])]});}
            var Q5;
            {var subQ1=sQuery(id+"F18.wireOp",EDGE,"E5");var subQ3=sQuery(id+"F18.wireOp",EDGE,"E4");var subQ5=makeQuery(id+"F18.imprint","INTERSECT",VERTEX,{"disambiguationData":[OD(1.0)],"derivedFrom":[subQ3,subQ1]});Q5=makeQuery(id+"F18.imprint","IMPRINT",FACE,{"disambiguationData":[TD([[makeQuery(id+"F18.imprint","IMPRINT",EDGE,{"disambiguationData":[TD([[subQ5,-1.0]])],"derivedFrom":subQ3}),1.0]])]});}
            extrude(context, id + "F42", {"entities" : qUnion([Q0, Q1, Q2, Q3, Q4, Q5]), "endBound" : BoundingType.SYMMETRIC, "depth" : 5.08 * mm});
        }
        {
            var Q0;
            Q0=qCreatedBy(makeId("Front.planeOp"),FACE);
            var sketch = newSketch(context, id + "F43", { "sketchPlane" : qUnion([Q0])});
            skCircle(sketch, "E13", {"center": v(0, 61.5) * mm, "radius": 2.78 * mm});
            skSolve(sketch);
        }
        {
            var Q0;
            Q0=makeQuery(id+"F43.imprint","IMPRINT",FACE,{"disambiguationData":[TD([[makeQuery(id+"F43.imprint","IMPRINT",EDGE,{"derivedFrom":sQuery(id+"F43.wireOp",EDGE,"E13")}),1.0]])]});
            extrude(context, id + "F44", {"entities" : qUnion([Q0]), "endBound" : BoundingType.SYMMETRIC, "depth" : 5.08 * mm});
        }
        {
            var Q0;
            Q0=qCreatedBy(makeId("Front.planeOp"),FACE);
            var sketch = newSketch(context, id + "F45", { "sketchPlane" : qUnion([Q0])});
            skLineSegment(sketch, "E14.rect.bottom", {"start": v(-5.44, 62.43) * mm, "end": v(5.44, 62.43) * mm});
            skLineSegment(sketch, "E14.rect.top", {"start": v(-5.44, 60.11) * mm, "end": v(5.44, 60.11) * mm});
            skLineSegment(sketch, "E14.rect.left", {"start": v(-5.44, 62.43) * mm, "end": v(-5.44, 60.11) * mm});
            skLineSegment(sketch, "E14.rect.right", {"start": v(5.44, 62.43) * mm, "end": v(5.44, 60.11) * mm});
            skPoint(sketch, "E14.rect.middle", {"position": v(0, 61.27) * mm});
            skSolve(sketch);
        }
        {
            var Q0;
            Q0 = qSketchRegion(id + "F45", true);
            extrude(context, id + "F46", {"entities" : qUnion([Q0]), "endBound" : BoundingType.SYMMETRIC, "depth" : 2.54 * mm});
        }
        {
            var Q0;
            {var subQ0=sQuery(id+"F18.wireOp",EDGE,"E4");Q0=makeQuery(id+"F25.opShell","OFFSET_EDGE",EDGE,{"disambiguationData":[OSD([subQ0]),TDD([makeQuery(id+"F19.opExtrude","CAP_EDGE",EDGE,{"disambiguationData":[OSD([subQ0]),TDD([makeQuery(id+"F18.imprint","IMPRINT",EDGE,{"disambiguationData":[TD([[makeQuery(id+"F18.imprint","INTERSECT",VERTEX,{"disambiguationData":[OD(2.0)],"derivedFrom":[subQ0,sQuery(id+"F18.wireOp",EDGE,"E6")]}),-1.0]])],"derivedFrom":subQ0})])],"isStart":true})])]});}
            var Q1;
            {var subQ0=sQuery(id+"F18.wireOp",EDGE,"E6");Q1=makeQuery(id+"F25.opShell","OFFSET_EDGE",EDGE,{"disambiguationData":[OSD([subQ0]),TDD([makeQuery(id+"F19.opExtrude","CAP_EDGE",EDGE,{"disambiguationData":[OSD([subQ0]),TDD([makeQuery(id+"F18.imprint","IMPRINT",EDGE,{"disambiguationData":[TD([[makeQuery(id+"F18.imprint","INTERSECT",VERTEX,{"disambiguationData":[OD(2.0)],"derivedFrom":[sQuery(id+"F18.wireOp",EDGE,"E4"),subQ0]}),1.0]])],"derivedFrom":subQ0})])],"isStart":true})])]});}
            var Q2;
            {var subQ0=sQuery(id+"F18.wireOp",EDGE,"E5");Q2=makeQuery(id+"F25.opShell","OFFSET_EDGE",EDGE,{"disambiguationData":[OSD([subQ0]),TDD([makeQuery(id+"F19.opExtrude","CAP_EDGE",EDGE,{"disambiguationData":[OSD([subQ0]),TDD([makeQuery(id+"F18.imprint","IMPRINT",EDGE,{"disambiguationData":[TD([[makeQuery(id+"F18.imprint","INTERSECT",VERTEX,{"disambiguationData":[OD(3.0)],"derivedFrom":[sQuery(id+"F18.wireOp",EDGE,"E4"),subQ0]}),-1.0]])],"derivedFrom":subQ0})])],"isStart":true})])]});}
            var Q3;
            {var subQ0=sQuery(id+"F18.wireOp",EDGE,"E4");Q3=makeQuery(id+"F25.opShell","OFFSET_EDGE",EDGE,{"disambiguationData":[OSD([subQ0]),TDD([makeQuery(id+"F19.opExtrude","CAP_EDGE",EDGE,{"disambiguationData":[OSD([subQ0]),TDD([makeQuery(id+"F18.imprint","IMPRINT",EDGE,{"disambiguationData":[TD([[makeQuery(id+"F18.imprint","INTERSECT",VERTEX,{"disambiguationData":[OD(3.0)],"derivedFrom":[subQ0,sQuery(id+"F18.wireOp",EDGE,"E6")]}),-1.0]])],"derivedFrom":subQ0})])],"isStart":true})])]});}
            var Q4;
            {var subQ0=sQuery(id+"F18.wireOp",EDGE,"E6");Q4=makeQuery(id+"F25.opShell","OFFSET_EDGE",EDGE,{"disambiguationData":[OSD([subQ0]),TDD([makeQuery(id+"F19.opExtrude","CAP_EDGE",EDGE,{"disambiguationData":[OSD([subQ0]),TDD([makeQuery(id+"F18.imprint","IMPRINT",EDGE,{"disambiguationData":[TD([[makeQuery(id+"F18.imprint","INTERSECT",VERTEX,{"disambiguationData":[OD(3.0)],"derivedFrom":[sQuery(id+"F18.wireOp",EDGE,"E4"),subQ0]}),1.0]])],"derivedFrom":subQ0})])],"isStart":true})])]});}
            var Q5;
            {var subQ0=sQuery(id+"F18.wireOp",EDGE,"E5");Q5=makeQuery(id+"F25.opShell","OFFSET_EDGE",EDGE,{"disambiguationData":[OSD([subQ0]),TDD([makeQuery(id+"F19.opExtrude","CAP_EDGE",EDGE,{"disambiguationData":[OSD([subQ0]),TDD([makeQuery(id+"F18.imprint","IMPRINT",EDGE,{"disambiguationData":[TD([[makeQuery(id+"F18.imprint","INTERSECT",VERTEX,{"disambiguationData":[OD(2.0)],"derivedFrom":[sQuery(id+"F18.wireOp",EDGE,"E4"),subQ0]}),-1.0]])],"derivedFrom":subQ0})])],"isStart":true})])]});}
            var Q6;
            {var subQ0=sQuery(id+"F18.wireOp",EDGE,"E6");Q6=makeQuery(id+"F25.opShell","OFFSET_EDGE",EDGE,{"disambiguationData":[OSD([subQ0]),TDD([makeQuery(id+"F19.opExtrude","CAP_EDGE",EDGE,{"disambiguationData":[OSD([subQ0]),TDD([makeQuery(id+"F18.imprint","IMPRINT",EDGE,{"disambiguationData":[TD([[makeQuery(id+"F18.imprint","INTERSECT",VERTEX,{"disambiguationData":[OD(2.0)],"derivedFrom":[sQuery(id+"F18.wireOp",EDGE,"E4"),subQ0]}),1.0]])],"derivedFrom":subQ0})])],"isStart":false})])]});}
            var Q7;
            {var subQ0=sQuery(id+"F18.wireOp",EDGE,"E4");Q7=makeQuery(id+"F25.opShell","OFFSET_EDGE",EDGE,{"disambiguationData":[OSD([subQ0]),TDD([makeQuery(id+"F19.opExtrude","CAP_EDGE",EDGE,{"disambiguationData":[OSD([subQ0]),TDD([makeQuery(id+"F18.imprint","IMPRINT",EDGE,{"disambiguationData":[TD([[makeQuery(id+"F18.imprint","INTERSECT",VERTEX,{"disambiguationData":[OD(2.0)],"derivedFrom":[subQ0,sQuery(id+"F18.wireOp",EDGE,"E6")]}),-1.0]])],"derivedFrom":subQ0})])],"isStart":false})])]});}
            var Q8;
            {var subQ0=sQuery(id+"F18.wireOp",EDGE,"E5");Q8=makeQuery(id+"F25.opShell","OFFSET_EDGE",EDGE,{"disambiguationData":[OSD([subQ0]),TDD([makeQuery(id+"F19.opExtrude","CAP_EDGE",EDGE,{"disambiguationData":[OSD([subQ0]),TDD([makeQuery(id+"F18.imprint","IMPRINT",EDGE,{"disambiguationData":[TD([[makeQuery(id+"F18.imprint","INTERSECT",VERTEX,{"disambiguationData":[OD(2.0)],"derivedFrom":[sQuery(id+"F18.wireOp",EDGE,"E4"),subQ0]}),-1.0]])],"derivedFrom":subQ0})])],"isStart":false})])]});}
            var Q9;
            {var subQ0=sQuery(id+"F18.wireOp",EDGE,"E6");Q9=makeQuery(id+"F25.opShell","OFFSET_EDGE",EDGE,{"disambiguationData":[OSD([subQ0]),TDD([makeQuery(id+"F19.opExtrude","CAP_EDGE",EDGE,{"disambiguationData":[OSD([subQ0]),TDD([makeQuery(id+"F18.imprint","IMPRINT",EDGE,{"disambiguationData":[TD([[makeQuery(id+"F18.imprint","INTERSECT",VERTEX,{"disambiguationData":[OD(3.0)],"derivedFrom":[sQuery(id+"F18.wireOp",EDGE,"E4"),subQ0]}),1.0]])],"derivedFrom":subQ0})])],"isStart":false})])]});}
            var Q10;
            {var subQ0=sQuery(id+"F18.wireOp",EDGE,"E4");Q10=makeQuery(id+"F25.opShell","OFFSET_EDGE",EDGE,{"disambiguationData":[OSD([subQ0]),TDD([makeQuery(id+"F19.opExtrude","CAP_EDGE",EDGE,{"disambiguationData":[OSD([subQ0]),TDD([makeQuery(id+"F18.imprint","IMPRINT",EDGE,{"disambiguationData":[TD([[makeQuery(id+"F18.imprint","INTERSECT",VERTEX,{"disambiguationData":[OD(3.0)],"derivedFrom":[subQ0,sQuery(id+"F18.wireOp",EDGE,"E6")]}),-1.0]])],"derivedFrom":subQ0})])],"isStart":false})])]});}
            var Q11;
            {var subQ0=sQuery(id+"F18.wireOp",EDGE,"E5");Q11=makeQuery(id+"F25.opShell","OFFSET_EDGE",EDGE,{"disambiguationData":[OSD([subQ0]),TDD([makeQuery(id+"F19.opExtrude","CAP_EDGE",EDGE,{"disambiguationData":[OSD([subQ0]),TDD([makeQuery(id+"F18.imprint","IMPRINT",EDGE,{"disambiguationData":[TD([[makeQuery(id+"F18.imprint","INTERSECT",VERTEX,{"disambiguationData":[OD(3.0)],"derivedFrom":[sQuery(id+"F18.wireOp",EDGE,"E4"),subQ0]}),-1.0]])],"derivedFrom":subQ0})])],"isStart":false})])]});}
            fillet(context, id + "F47", {"entities" : qUnion([Q0, Q1, Q2, Q3, Q4, Q5, Q6, Q7, Q8, Q9, Q10, Q11]), "radius" : 1.27 * mm, "tangentPropagation" : true, "allowEdgeOverflow" : false});
        }
        {
            var Q0;
            Q0=makeQuery(id+"F1.opExtrude","SWEPT_EDGE",EDGE,{"disambiguationData":[OSD([sQuery(id+"F0.wireOp",EDGE,"E0.rect.top"),sQuery(id+"F0.wireOp",EDGE,"E0.rect.left")])]});
            var Q1;
            Q1=makeQuery(id+"F1.opExtrude","SWEPT_EDGE",EDGE,{"disambiguationData":[OSD([sQuery(id+"F0.wireOp",EDGE,"E0.rect.bottom"),sQuery(id+"F0.wireOp",EDGE,"E0.rect.left")])]});
            var Q2;
            Q2=makeQuery(id+"F1.opExtrude","SWEPT_EDGE",EDGE,{"disambiguationData":[OSD([sQuery(id+"F0.wireOp",EDGE,"E0.rect.bottom"),sQuery(id+"F0.wireOp",EDGE,"E0.rect.right")])]});
            var Q3;
            Q3=makeQuery(id+"F1.opExtrude","SWEPT_EDGE",EDGE,{"disambiguationData":[OSD([sQuery(id+"F0.wireOp",EDGE,"E0.rect.top"),sQuery(id+"F0.wireOp",EDGE,"E0.rect.right")])]});
            chamfer(context, id + "F48", {"entities" : qUnion([Q0, Q1, Q2, Q3]), "width" : 5.08 * mm, "tangentPropagation" : true});
        }
        {
            var Q0;
            Q0=makeQuery(id+"F36.opExtrude","CAP_EDGE",EDGE,{"disambiguationData":[OSD([sQuery(id+"F35.wireOp",EDGE,"E10")])],"isStart":false});
            chamfer(context, id + "F49", {"entities" : qUnion([Q0]), "width" : 3.05 * mm, "tangentPropagation" : true});
        }
        {
            var Q0;
            Q0=makeQuery(id+"F38.opExtrude","CAP_EDGE",EDGE,{"disambiguationData":[OSD([sQuery(id+"F37.wireOp",EDGE,"E11")])],"isStart":false});
            var Q1;
            Q1=makeQuery(id+"F38.opExtrude","CAP_EDGE",EDGE,{"disambiguationData":[OSD([sQuery(id+"F37.wireOp",EDGE,"E11")])],"isStart":true});
            chamfer(context, id + "F50", {"entities" : qUnion([Q0, Q1]), "width" : 2.3 * mm, "tangentPropagation" : true});
        }
        {
            var Q0;
            Q0=makeQuery(id+"F40.opExtrude","CAP_EDGE",EDGE,{"disambiguationData":[OSD([sQuery(id+"F39.wireOp",EDGE,"E12")])],"isStart":false});
            var Q1;
            Q1=makeQuery(id+"F40.opExtrude","CAP_EDGE",EDGE,{"disambiguationData":[OSD([sQuery(id+"F39.wireOp",EDGE,"E12")])],"isStart":true});
            chamfer(context, id + "F51", {"entities" : qUnion([Q0, Q1]), "width" : 1.27 * mm, "tangentPropagation" : true});
        }
        {
            var Q0;
            {var subQ0=sQuery(id+"F26.wireOp",EDGE,"E8.rect.top");var subQ1=sQuery(id+"F26.wireOp",EDGE,"E8.rect.left");Q0=makeQuery(id+"F29.opShell","OFFSET_EDGE",EDGE,{"disambiguationData":[OSD([subQ0,subQ1]),TDD([makeQuery(id+"F28.opFillet","BLEND_EDGE",EDGE,{"blendedFrom":[makeQuery(id+"F27.opExtrude","CAP_EDGE",EDGE,{"disambiguationData":[OSD([subQ0])],"isStart":false}),makeQuery(id+"F27.opExtrude","SWEPT_FACE",FACE,{"disambiguationData":[OSD([subQ1])]})],"blendedInto":[makeQuery(id+"F27.opExtrude","SWEPT_FACE",FACE,{"disambiguationData":[OSD([subQ1])]})]})])]});}
            var Q1;
            Q1=makeQuery(id+"F28.opFillet","BLEND_EDGE",EDGE,{"blendedFrom":[makeQuery(id+"F27.opExtrude","CAP_EDGE",EDGE,{"disambiguationData":[OSD([sQuery(id+"F26.wireOp",EDGE,"E8.rect.top")])],"isStart":false}),makeQuery(id+"F27.opExtrude","SWEPT_FACE",FACE,{"disambiguationData":[OSD([sQuery(id+"F26.wireOp",EDGE,"E8.rect.left")])]})],"blendedInto":[makeQuery(id+"F27.opExtrude","SWEPT_FACE",FACE,{"disambiguationData":[OSD([sQuery(id+"F26.wireOp",EDGE,"E8.rect.left")])]})]});
            var Q2;
            Q2=makeQuery(id+"F28.opFillet","BLEND_EDGE",EDGE,{"blendedFrom":[makeQuery(id+"F27.opExtrude","CAP_EDGE",EDGE,{"disambiguationData":[OSD([sQuery(id+"F26.wireOp",EDGE,"E8.rect.bottom")])],"isStart":false}),makeQuery(id+"F27.opExtrude","SWEPT_FACE",FACE,{"disambiguationData":[OSD([sQuery(id+"F26.wireOp",EDGE,"E8.rect.left")])]})],"blendedInto":[makeQuery(id+"F27.opExtrude","SWEPT_FACE",FACE,{"disambiguationData":[OSD([sQuery(id+"F26.wireOp",EDGE,"E8.rect.left")])]})]});
            var Q3;
            {var subQ0=sQuery(id+"F26.wireOp",EDGE,"E8.rect.bottom");var subQ1=sQuery(id+"F26.wireOp",EDGE,"E8.rect.left");Q3=makeQuery(id+"F29.opShell","OFFSET_EDGE",EDGE,{"disambiguationData":[OSD([subQ0,subQ1]),TDD([makeQuery(id+"F28.opFillet","BLEND_EDGE",EDGE,{"blendedFrom":[makeQuery(id+"F27.opExtrude","CAP_EDGE",EDGE,{"disambiguationData":[OSD([subQ0])],"isStart":false}),makeQuery(id+"F27.opExtrude","SWEPT_FACE",FACE,{"disambiguationData":[OSD([subQ1])]})],"blendedInto":[makeQuery(id+"F27.opExtrude","SWEPT_FACE",FACE,{"disambiguationData":[OSD([subQ1])]})]})])]});}
            var Q4;
            {var subQ0=sQuery(id+"F26.wireOp",EDGE,"E8.rect.top");var subQ1=sQuery(id+"F26.wireOp",EDGE,"E8.rect.left");Q4=makeQuery(id+"F29.opShell","OFFSET_EDGE",EDGE,{"disambiguationData":[OSD([subQ0,subQ1]),TDD([makeQuery(id+"F27.opExtrude","SWEPT_EDGE",EDGE,{"disambiguationData":[OSD([subQ0,subQ1])]})])]});}
            var Q5;
            Q5=makeQuery(id+"F27.opExtrude","SWEPT_EDGE",EDGE,{"disambiguationData":[OSD([sQuery(id+"F26.wireOp",EDGE,"E8.rect.top"),sQuery(id+"F26.wireOp",EDGE,"E8.rect.left")])]});
            var Q6;
            Q6=makeQuery(id+"F28.opFillet","BLEND_EDGE",EDGE,{"blendedFrom":[makeQuery(id+"F27.opExtrude","CAP_EDGE",EDGE,{"disambiguationData":[OSD([sQuery(id+"F26.wireOp",EDGE,"E8.rect.top")])],"isStart":true}),makeQuery(id+"F27.opExtrude","SWEPT_FACE",FACE,{"disambiguationData":[OSD([sQuery(id+"F26.wireOp",EDGE,"E8.rect.left")])]})],"blendedInto":[makeQuery(id+"F27.opExtrude","SWEPT_FACE",FACE,{"disambiguationData":[OSD([sQuery(id+"F26.wireOp",EDGE,"E8.rect.left")])]})]});
            var Q7;
            {var subQ0=sQuery(id+"F26.wireOp",EDGE,"E8.rect.top");var subQ1=sQuery(id+"F26.wireOp",EDGE,"E8.rect.left");Q7=makeQuery(id+"F29.opShell","OFFSET_EDGE",EDGE,{"disambiguationData":[OSD([subQ0,subQ1]),TDD([makeQuery(id+"F28.opFillet","BLEND_EDGE",EDGE,{"blendedFrom":[makeQuery(id+"F27.opExtrude","CAP_EDGE",EDGE,{"disambiguationData":[OSD([subQ0])],"isStart":true}),makeQuery(id+"F27.opExtrude","SWEPT_FACE",FACE,{"disambiguationData":[OSD([subQ1])]})],"blendedInto":[makeQuery(id+"F27.opExtrude","SWEPT_FACE",FACE,{"disambiguationData":[OSD([subQ1])]})]})])]});}
            var Q8;
            {var subQ0=sQuery(id+"F26.wireOp",EDGE,"E8.rect.bottom");var subQ1=sQuery(id+"F26.wireOp",EDGE,"E8.rect.left");Q8=makeQuery(id+"F29.opShell","OFFSET_EDGE",EDGE,{"disambiguationData":[OSD([subQ0,subQ1]),TDD([makeQuery(id+"F28.opFillet","BLEND_EDGE",EDGE,{"blendedFrom":[makeQuery(id+"F27.opExtrude","CAP_EDGE",EDGE,{"disambiguationData":[OSD([subQ0])],"isStart":true}),makeQuery(id+"F27.opExtrude","SWEPT_FACE",FACE,{"disambiguationData":[OSD([subQ1])]})],"blendedInto":[makeQuery(id+"F27.opExtrude","SWEPT_FACE",FACE,{"disambiguationData":[OSD([subQ1])]})]})])]});}
            var Q9;
            Q9=makeQuery(id+"F28.opFillet","BLEND_EDGE",EDGE,{"blendedFrom":[makeQuery(id+"F27.opExtrude","CAP_EDGE",EDGE,{"disambiguationData":[OSD([sQuery(id+"F26.wireOp",EDGE,"E8.rect.bottom")])],"isStart":true}),makeQuery(id+"F27.opExtrude","SWEPT_FACE",FACE,{"disambiguationData":[OSD([sQuery(id+"F26.wireOp",EDGE,"E8.rect.left")])]})],"blendedInto":[makeQuery(id+"F27.opExtrude","SWEPT_FACE",FACE,{"disambiguationData":[OSD([sQuery(id+"F26.wireOp",EDGE,"E8.rect.left")])]})]});
            var Q10;
            Q10=makeQuery(id+"F28.opFillet","BLEND_EDGE",EDGE,{"blendedFrom":[makeQuery(id+"F27.opExtrude","CAP_EDGE",EDGE,{"disambiguationData":[OSD([sQuery(id+"F26.wireOp",EDGE,"E8.rect.bottom")])],"isStart":true}),makeQuery(id+"F27.opExtrude","SWEPT_FACE",FACE,{"disambiguationData":[OSD([sQuery(id+"F26.wireOp",EDGE,"E8.rect.right")])]})],"blendedInto":[makeQuery(id+"F27.opExtrude","SWEPT_FACE",FACE,{"disambiguationData":[OSD([sQuery(id+"F26.wireOp",EDGE,"E8.rect.right")])]})]});
            var Q11;
            {var subQ0=sQuery(id+"F26.wireOp",EDGE,"E8.rect.bottom");var subQ1=sQuery(id+"F26.wireOp",EDGE,"E8.rect.right");Q11=makeQuery(id+"F29.opShell","OFFSET_EDGE",EDGE,{"disambiguationData":[OSD([subQ0,subQ1]),TDD([makeQuery(id+"F28.opFillet","BLEND_EDGE",EDGE,{"blendedFrom":[makeQuery(id+"F27.opExtrude","CAP_EDGE",EDGE,{"disambiguationData":[OSD([subQ0])],"isStart":true}),makeQuery(id+"F27.opExtrude","SWEPT_FACE",FACE,{"disambiguationData":[OSD([subQ1])]})],"blendedInto":[makeQuery(id+"F27.opExtrude","SWEPT_FACE",FACE,{"disambiguationData":[OSD([subQ1])]})]})])]});}
            var Q12;
            Q12=makeQuery(id+"F28.opFillet","BLEND_EDGE",EDGE,{"blendedFrom":[makeQuery(id+"F27.opExtrude","CAP_EDGE",EDGE,{"disambiguationData":[OSD([sQuery(id+"F26.wireOp",EDGE,"E8.rect.top")])],"isStart":true}),makeQuery(id+"F27.opExtrude","SWEPT_FACE",FACE,{"disambiguationData":[OSD([sQuery(id+"F26.wireOp",EDGE,"E8.rect.right")])]})],"blendedInto":[makeQuery(id+"F27.opExtrude","SWEPT_FACE",FACE,{"disambiguationData":[OSD([sQuery(id+"F26.wireOp",EDGE,"E8.rect.right")])]})]});
            var Q13;
            {var subQ0=sQuery(id+"F26.wireOp",EDGE,"E8.rect.top");var subQ1=sQuery(id+"F26.wireOp",EDGE,"E8.rect.right");Q13=makeQuery(id+"F29.opShell","OFFSET_EDGE",EDGE,{"disambiguationData":[OSD([subQ0,subQ1]),TDD([makeQuery(id+"F28.opFillet","BLEND_EDGE",EDGE,{"blendedFrom":[makeQuery(id+"F27.opExtrude","CAP_EDGE",EDGE,{"disambiguationData":[OSD([subQ0])],"isStart":true}),makeQuery(id+"F27.opExtrude","SWEPT_FACE",FACE,{"disambiguationData":[OSD([subQ1])]})],"blendedInto":[makeQuery(id+"F27.opExtrude","SWEPT_FACE",FACE,{"disambiguationData":[OSD([subQ1])]})]})])]});}
            var Q14;
            {var subQ0=sQuery(id+"F26.wireOp",EDGE,"E8.rect.top");var subQ1=sQuery(id+"F26.wireOp",EDGE,"E8.rect.right");Q14=makeQuery(id+"F29.opShell","OFFSET_EDGE",EDGE,{"disambiguationData":[OSD([subQ0,subQ1]),TDD([makeQuery(id+"F27.opExtrude","SWEPT_EDGE",EDGE,{"disambiguationData":[OSD([subQ0,subQ1])]})])]});}
            var Q15;
            Q15=makeQuery(id+"F27.opExtrude","SWEPT_EDGE",EDGE,{"disambiguationData":[OSD([sQuery(id+"F26.wireOp",EDGE,"E8.rect.top"),sQuery(id+"F26.wireOp",EDGE,"E8.rect.right")])]});
            var Q16;
            Q16=makeQuery(id+"F28.opFillet","BLEND_EDGE",EDGE,{"blendedFrom":[makeQuery(id+"F27.opExtrude","CAP_EDGE",EDGE,{"disambiguationData":[OSD([sQuery(id+"F26.wireOp",EDGE,"E8.rect.top")])],"isStart":false}),makeQuery(id+"F27.opExtrude","SWEPT_FACE",FACE,{"disambiguationData":[OSD([sQuery(id+"F26.wireOp",EDGE,"E8.rect.right")])]})],"blendedInto":[makeQuery(id+"F27.opExtrude","SWEPT_FACE",FACE,{"disambiguationData":[OSD([sQuery(id+"F26.wireOp",EDGE,"E8.rect.right")])]})]});
            var Q17;
            {var subQ0=sQuery(id+"F26.wireOp",EDGE,"E8.rect.top");var subQ1=sQuery(id+"F26.wireOp",EDGE,"E8.rect.right");Q17=makeQuery(id+"F29.opShell","OFFSET_EDGE",EDGE,{"disambiguationData":[OSD([subQ0,subQ1]),TDD([makeQuery(id+"F28.opFillet","BLEND_EDGE",EDGE,{"blendedFrom":[makeQuery(id+"F27.opExtrude","CAP_EDGE",EDGE,{"disambiguationData":[OSD([subQ0])],"isStart":false}),makeQuery(id+"F27.opExtrude","SWEPT_FACE",FACE,{"disambiguationData":[OSD([subQ1])]})],"blendedInto":[makeQuery(id+"F27.opExtrude","SWEPT_FACE",FACE,{"disambiguationData":[OSD([subQ1])]})]})])]});}
            var Q18;
            Q18=makeQuery(id+"F28.opFillet","BLEND_EDGE",EDGE,{"blendedFrom":[makeQuery(id+"F27.opExtrude","CAP_EDGE",EDGE,{"disambiguationData":[OSD([sQuery(id+"F26.wireOp",EDGE,"E8.rect.bottom")])],"isStart":false}),makeQuery(id+"F27.opExtrude","SWEPT_FACE",FACE,{"disambiguationData":[OSD([sQuery(id+"F26.wireOp",EDGE,"E8.rect.right")])]})],"blendedInto":[makeQuery(id+"F27.opExtrude","SWEPT_FACE",FACE,{"disambiguationData":[OSD([sQuery(id+"F26.wireOp",EDGE,"E8.rect.right")])]})]});
            var Q19;
            {var subQ0=sQuery(id+"F26.wireOp",EDGE,"E8.rect.bottom");var subQ1=sQuery(id+"F26.wireOp",EDGE,"E8.rect.right");Q19=makeQuery(id+"F29.opShell","OFFSET_EDGE",EDGE,{"disambiguationData":[OSD([subQ0,subQ1]),TDD([makeQuery(id+"F28.opFillet","BLEND_EDGE",EDGE,{"blendedFrom":[makeQuery(id+"F27.opExtrude","CAP_EDGE",EDGE,{"disambiguationData":[OSD([subQ0])],"isStart":false}),makeQuery(id+"F27.opExtrude","SWEPT_FACE",FACE,{"disambiguationData":[OSD([subQ1])]})],"blendedInto":[makeQuery(id+"F27.opExtrude","SWEPT_FACE",FACE,{"disambiguationData":[OSD([subQ1])]})]})])]});}
            fillet(context, id + "F52", {"entities" : qUnion([Q0, Q1, Q2, Q3, Q4, Q5, Q6, Q7, Q8, Q9, Q10, Q11, Q12, Q13, Q14, Q15, Q16, Q17, Q18, Q19]), "radius" : 1.9 * mm, "tangentPropagation" : true, "allowEdgeOverflow" : false});
        }
        {
            var Q0;
            {var subQ0=sQuery(id+"F35.wireOp",EDGE,"E10");Q0=makeQuery(id+"F49.opChamfer","BLEND_EDGE",EDGE,{"blendedFrom":[makeQuery(id+"F36.opExtrude","CAP_EDGE",EDGE,{"disambiguationData":[OSD([subQ0])],"isStart":false}),makeQuery(id+"F36.opExtrude","SWEPT_FACE",FACE,{"disambiguationData":[OSD([subQ0])]})],"blendedInto":[makeQuery(id+"F36.opExtrude","SWEPT_FACE",FACE,{"disambiguationData":[OSD([subQ0])]})]});}
            fillet(context, id + "F53", {"entities" : qUnion([Q0]), "radius" : 12.7 * mm, "tangentPropagation" : true, "allowEdgeOverflow" : false});
        }
        {
            var Q0;
            Q0=makeQuery(id+"F32.opChamfer","BLEND_EDGE",EDGE,{"blendedFrom":[makeQuery(id+"F31.opExtrude","CAP_EDGE",EDGE,{"disambiguationData":[OSD([sQuery(id+"F30.wireOp",EDGE,"E9.rect.bottom")])],"isStart":true}),makeQuery(id+"F31.opExtrude","CAP_EDGE",EDGE,{"disambiguationData":[OSD([sQuery(id+"F30.wireOp",EDGE,"E9.rect.left")])],"isStart":true})],"blendedInto":[]});
            var Q1;
            Q1=makeQuery(id+"F32.opChamfer","BLEND_EDGE",EDGE,{"blendedFrom":[makeQuery(id+"F31.opExtrude","CAP_EDGE",EDGE,{"disambiguationData":[OSD([sQuery(id+"F30.wireOp",EDGE,"E9.rect.bottom")])],"isStart":true}),makeQuery(id+"F31.opExtrude","CAP_EDGE",EDGE,{"disambiguationData":[OSD([sQuery(id+"F30.wireOp",EDGE,"E9.rect.right")])],"isStart":true})],"blendedInto":[]});
            var Q2;
            Q2=makeQuery(id+"F32.opChamfer","BLEND_EDGE",EDGE,{"blendedFrom":[makeQuery(id+"F31.opExtrude","CAP_EDGE",EDGE,{"disambiguationData":[OSD([sQuery(id+"F30.wireOp",EDGE,"E9.rect.top")])],"isStart":true}),makeQuery(id+"F31.opExtrude","CAP_EDGE",EDGE,{"disambiguationData":[OSD([sQuery(id+"F30.wireOp",EDGE,"E9.rect.right")])],"isStart":true})],"blendedInto":[]});
            var Q3;
            Q3=makeQuery(id+"F32.opChamfer","BLEND_EDGE",EDGE,{"blendedFrom":[makeQuery(id+"F31.opExtrude","CAP_EDGE",EDGE,{"disambiguationData":[OSD([sQuery(id+"F30.wireOp",EDGE,"E9.rect.top")])],"isStart":true}),makeQuery(id+"F31.opExtrude","CAP_EDGE",EDGE,{"disambiguationData":[OSD([sQuery(id+"F30.wireOp",EDGE,"E9.rect.left")])],"isStart":true})],"blendedInto":[]});
            chamfer(context, id + "F54", {"entities" : qUnion([Q0, Q1, Q2, Q3]), "width" : 1.27 * mm, "tangentPropagation" : true});
        }
    });
